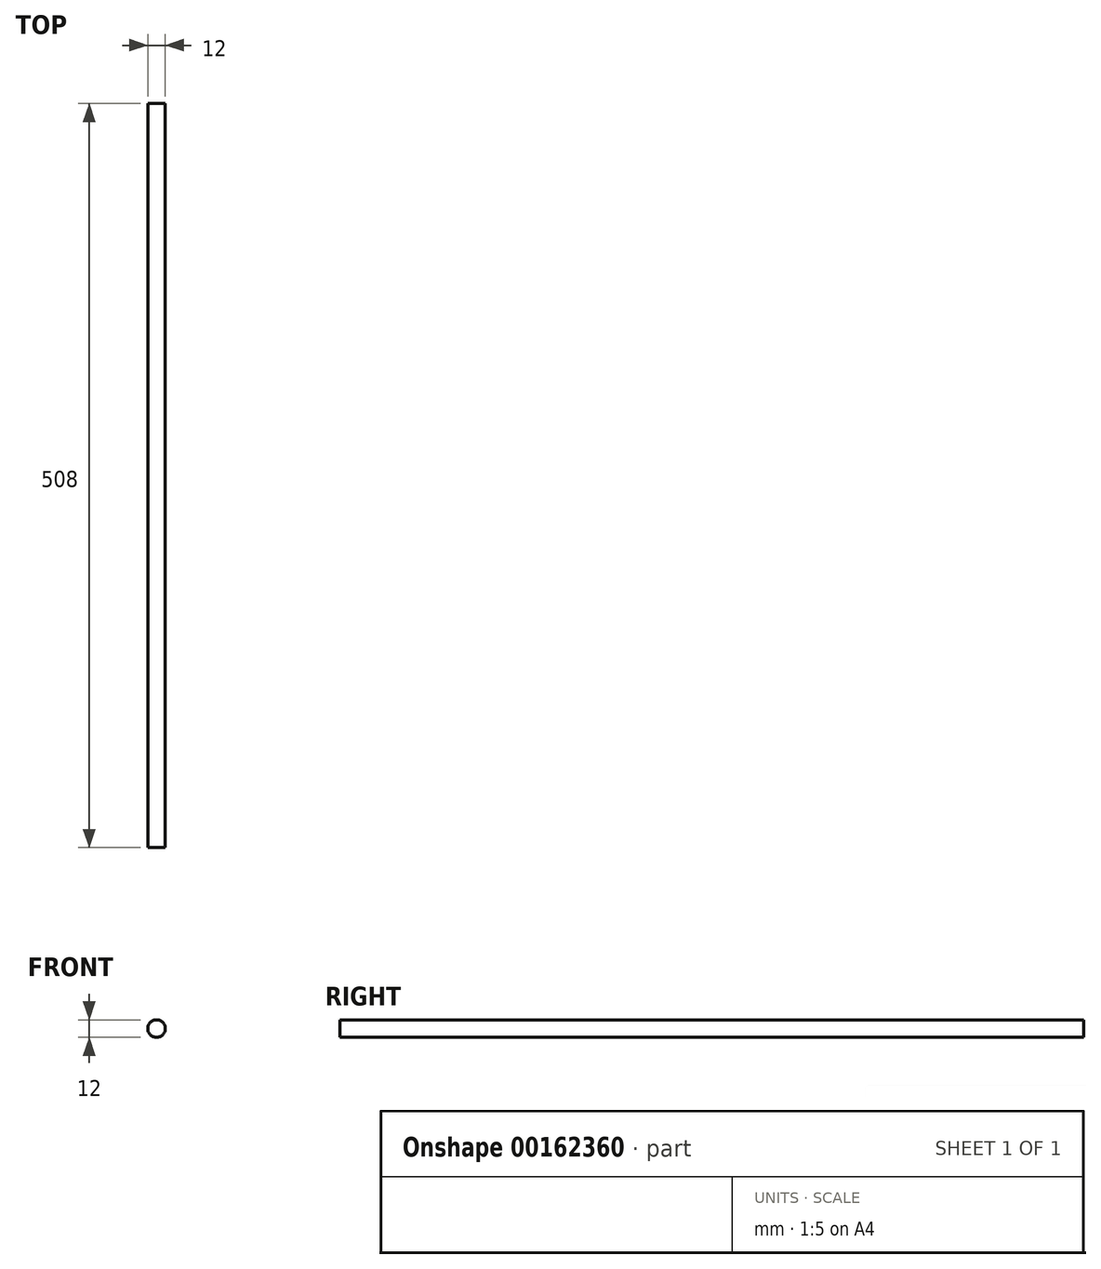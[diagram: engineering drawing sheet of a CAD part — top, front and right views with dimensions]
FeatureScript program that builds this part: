
annotation { "Feature Type Name" : "Feature", "Feature Type Description" : "" }
export const myFeature = defineFeature(function(context is Context, id is Id, definition is map)
    precondition{}
    {
        {
            var Q0;
            Q0=qCreatedBy(makeId("Front.planeOp"),FACE);
            var sketch = newSketch(context, id + "F0", { "sketchPlane" : qUnion([Q0])});
            skCircle(sketch, "E0", {"center": v(0, 0) * mm, "radius": 6 * mm});
            skSolve(sketch);
        }
        {
            var Q0;
            Q0 = qSketchRegion(id + "F0", true);
            extrude(context, id + "F1", {"entities" : qUnion([Q0]), "depth" : 508 * mm});
        }
    });
